# Revit family: 0047964 Sylvania Lighting Fixture START eco Flood Flat IP65 2800lm 830
name_source: partatom
category: Lighting Fixtures
revit_build: Autodesk Revit 2016 (Build: 20150220_1215(x64)
units: mm (PartAtom-declared; Revit-internal decimal feet)

## family parameters
Cut with Voids When Loaded = No
Host = Face
Light Source = No
OmniClass Number = 23.80.70.00
OmniClass Title = Lighting
Part Type = Normal
Room Calculation Point = No
Round Connector Dimension = Use Diameter
Shared = No

## types (1)
- 0047964 ST E FLD FLT IP65 2800LM 830
    10W_SYL = No
    30W_SYL = Yes
    50W_SYL = No
    Apparent Load = 30 VA
    Assembly Code = D5020200
    AssetType = Fixed
    ClassificationName = Uniclass2015
    ClassificationValue = EF_70_80
    Cost = 0 $
    Default Elevation = 1219 mm
    DepthBracket_SYL = 15 mm  [stored 0.0492126 ft]
    Description = The new Start eco Flood Flat comes with improved design. The streamlined, durable, lightweight die-cast aluminium body makes it a perfect choice for building facades, car parks, garages and construction areas. The product includes 1 m pre-wired stripped cable and fitting bracket for quick and easy installation and the universal mounting bracket allows wall or surface mounting with the possibility of vertical tilting. Black die-cast aluminum housing, white reflector, 2700 lm, 30 W, 90 lm/W, 3000K, drive current 116 mA, non dimmable, CRI>80, IP65, IK06, Class I, lumen maintenance L70:B50: 30000 hrs, 156 x 126 x 38 mm (L x W x H). Weight: 0.545kg. Energy class: A++ A+ A.
    DocumentationLiterature = http://www.sylvania-lighting.com
    DurationUnit = hours
    ElectricShockClassification = Class I
    ExpectedLife = 30000
    HeightBracket_SYL = 70 mm  [stored 0.229659 ft]
    IfcExportAs = IfcLightFixtureType
    IfcExportType = IfcLightFixtureType
    ImpactProtectionIndex = IK06
    IngressProtection = IP65
    Keynote = 16500
    Lamp = LED
    LampColourRenderingIndex = 80
    LampColourTemperature = 3000 K
    LampNominalLuminous = 2700 lm
    LampsType = LED
    LuminousEfficacy = 90 lm/W
    Manufacturer = Feilo Sylvania
    ManufacturerName = Feilo Sylvania
    Material = adc12 housing
    Material_1_SYL = Body-Sylvania-FloodFlat-Black
    Model = START eco Flood Flat IP65 2800lm 830
    ModelNumber = 0047964
    ModelReference = START eco Flood Flat IP65 2800lm 830
    Name = START eco Flood Flat IP65 2800lm 830
    NominalDepth = 126 mm  [stored 0.413386 ft]
    NominalHeight = 38 mm  [stored 0.124672 ft]
    NominalLength = 156 mm  [stored 0.511811 ft]
    OffsetAxis_SYL = 8 mm  [stored 0.0262467 ft]
    PowerConsumption = 30 W
    PowerFactor = 0.9
    RadiusBracketIn_SYL = 6 mm  [stored 0.019685 ft]
    RadiusBracket_SYL = 8 mm  [stored 0.0262467 ft]
    ThicknessBracket_SYL = 2 mm  [stored 0.00656168 ft]
    Type Image = <None>
    TypeLight_SYL = START eco Flood Flat Lamp : 0047964 ST E FLD FLT IP65 2800LM 830
    TypeName = START eco Flood Flat IP65 2800lm 830
    URL = http://www.sylvania-lighting.com
    Voltage = 0 V
    Weight = 6.54 kg
    WidthBracketIn_SYL = 143 mm

note: [stored X ft] marks values corroborated as IEEE doubles in the binary element streams (Revit-internal decimal feet)

## geometry (parser evidence)
native form markers: Sweep x5
no freeform markers — native parametric forms only
